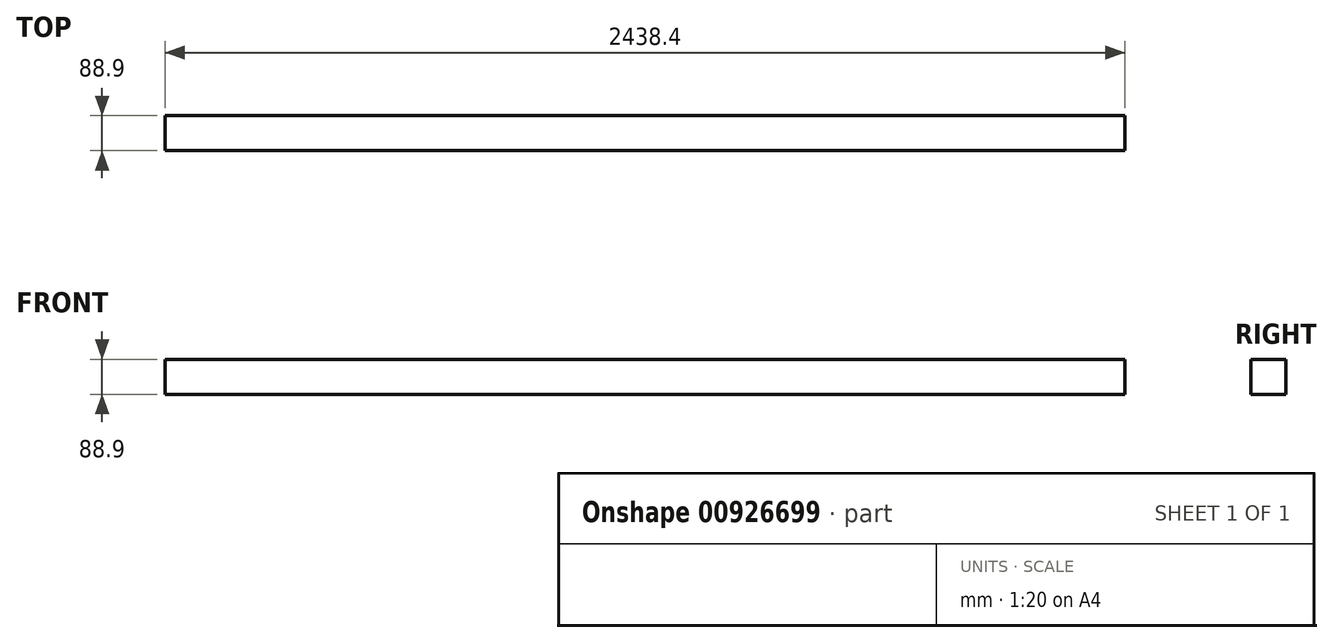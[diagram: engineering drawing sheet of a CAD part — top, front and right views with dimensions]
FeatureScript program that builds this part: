
annotation { "Feature Type Name" : "Feature", "Feature Type Description" : "" }
export const myFeature = defineFeature(function(context is Context, id is Id, definition is map)
    precondition{}
    {
        {
            var Q0;
            Q0=qCreatedBy(makeId("Right.planeOp"),FACE);
            var sketch = newSketch(context, id + "F0", { "sketchPlane" : qUnion([Q0])});
            skLineSegment(sketch, "E0.bottom", {"start": v(44.45, 44.45) * mm, "end": v(-44.45, 44.45) * mm});
            skLineSegment(sketch, "E0.top", {"start": v(44.45, -44.45) * mm, "end": v(-44.45, -44.45) * mm});
            skLineSegment(sketch, "E0.left", {"start": v(44.45, 44.45) * mm, "end": v(44.45, -44.45) * mm});
            skLineSegment(sketch, "E0.right", {"start": v(-44.45, 44.45) * mm, "end": v(-44.45, -44.45) * mm});
            skPoint(sketch, "E0.middle", {"position": v(0, 0) * mm});
            skSolve(sketch);
        }
        {
            var Q0;
            Q0=makeQuery(id+"F0.imprint","IMPRINT",FACE,{"disambiguationData":[TD([[makeQuery(id+"F0.imprint","IMPRINT",EDGE,{"derivedFrom":sQuery(id+"F0.wireOp",EDGE,"E0.bottom")}),1.0]])]});
            extrude(context, id + "F1", {"entities" : qUnion([Q0]), "depth" : 2438.4 * mm, "offsetDistance" : 25.4 * mm});
        }
    });
